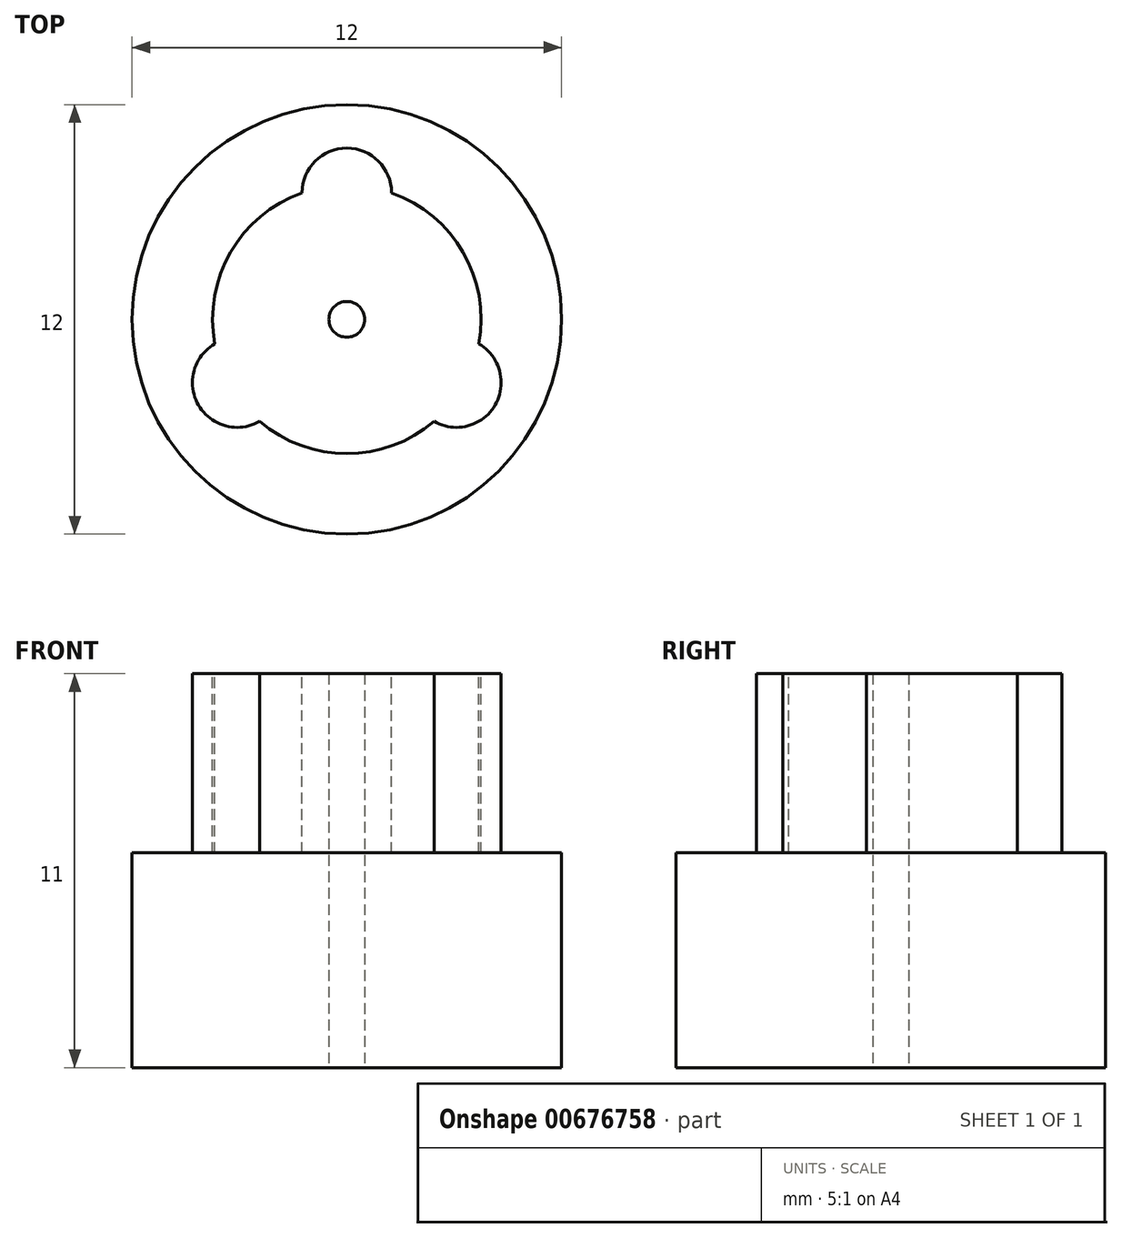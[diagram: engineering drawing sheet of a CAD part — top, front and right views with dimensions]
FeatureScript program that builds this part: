
annotation { "Feature Type Name" : "Feature", "Feature Type Description" : "" }
export const myFeature = defineFeature(function(context is Context, id is Id, definition is map)
    precondition{}
    {
        {
            var Q0;
            Q0=qCreatedBy(makeId("Top.planeOp"),FACE);
            var sketch = newSketch(context, id + "F0", { "sketchPlane" : qUnion([Q0])});
            skCircle(sketch, "E0", {"center": v(0, 0) * mm, "radius": 6 * mm});
            skCircle(sketch, "E1", {"center": v(0, 0) * mm, "radius": 0.5 * mm});
            skSolve(sketch);
        }
        {
            var Q0;
            Q0=makeQuery(id+"F0.imprint","IMPRINT",FACE,{"disambiguationData":[TD([[makeQuery(id+"F0.imprint","IMPRINT",EDGE,{"derivedFrom":sQuery(id+"F0.wireOp",EDGE,"E0")}),1.0]])]});
            extrude(context, id + "F1", {"entities" : qUnion([Q0]), "depth" : 11 * mm, "offsetDistance" : 25 * mm});
        }
        {
            var Q0;
            Q0=makeQuery(id+"F1.opExtrude","CAP_FACE",FACE,{"disambiguationData":[OSD([sQuery(id+"F0.wireOp",EDGE,"E0"),sQuery(id+"F0.wireOp",EDGE,"E1")])],"isStart":false});
            var sketch = newSketch(context, id + "F2", { "sketchPlane" : qUnion([Q0])});
            skArc(sketch, "E2", {"start": v(-3.69, -0.69) * mm, "mid": v(-3.25, 1.88) * mm, "end": v(-1.25, 3.54) * mm});
            skArc(sketch, "E3", {"start": v(-1.25, 3.54) * mm, "mid": v(0, 4.79) * mm, "end": v(1.25, 3.54) * mm});
            skArc(sketch, "E4.1.0", {"start": v(2.44, -2.85) * mm, "mid": v(0, -3.75) * mm, "end": v(-2.44, -2.85) * mm});
            skArc(sketch, "E4.1.1", {"start": v(-2.44, -2.85) * mm, "mid": v(-4.14, -2.4) * mm, "end": v(-3.69, -0.69) * mm});
            skArc(sketch, "E4.2.0", {"start": v(1.25, 3.54) * mm, "mid": v(3.25, 1.87) * mm, "end": v(3.69, -0.69) * mm});
            skArc(sketch, "E4.2.1", {"start": v(3.69, -0.69) * mm, "mid": v(4.14, -2.4) * mm, "end": v(2.44, -2.85) * mm});
            skSolve(sketch);
        }
        {
            var Q0;
            Q0=makeQuery(id+"F2.imprint","IMPRINT",FACE,{"disambiguationData":[TD([[makeQuery(id+"F2.imprint","IMPRINT",EDGE,{"derivedFrom":sQuery(id+"F2.wireOp",EDGE,"E2")}),-1.0]])]});
            extrude(context, id + "F3", {"entities" : qUnion([Q0]), "operationType" : NewBodyOperationType.REMOVE, "oppositeDirection" : true, "depth" : 5 * mm, "offsetDistance" : 25 * mm});
        }
    });
